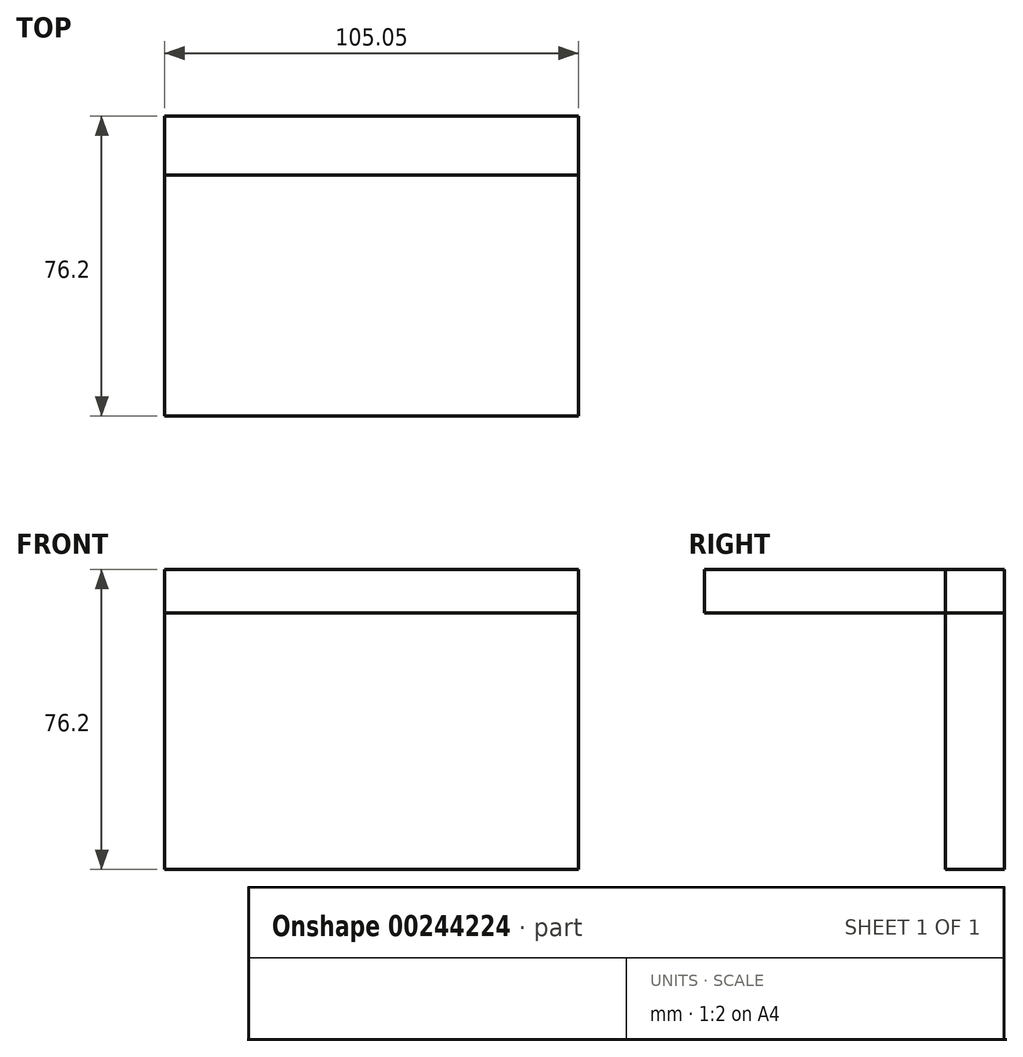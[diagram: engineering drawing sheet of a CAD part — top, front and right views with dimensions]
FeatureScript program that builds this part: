
annotation { "Feature Type Name" : "Feature", "Feature Type Description" : "" }
export const myFeature = defineFeature(function(context is Context, id is Id, definition is map)
    precondition{}
    {
        {
            var Q0;
            Q0=qCreatedBy(makeId("Front.planeOp"),FACE);
            var sketch = newSketch(context, id + "F0", { "sketchPlane" : qUnion([Q0])});
            skLineSegment(sketch, "E0.bottom", {"start": v(-63.6, 52.39) * mm, "end": v(41.45, 52.39) * mm});
            skLineSegment(sketch, "E0.top", {"start": v(-63.6, 41.31) * mm, "end": v(41.45, 41.31) * mm});
            skLineSegment(sketch, "E0.left", {"start": v(-63.6, 52.39) * mm, "end": v(-63.6, 41.31) * mm});
            skLineSegment(sketch, "E0.right", {"start": v(41.45, 52.39) * mm, "end": v(41.45, 41.31) * mm});
            skSolve(sketch);
        }
        {
            var Q0;
            Q0 = qSketchRegion(id + "F0", true);
            extrude(context, id + "F1", {"entities" : qUnion([Q0]), "depth" : 76.2 * mm});
        }
        {
            var Q0;
            Q0=makeQuery(id+"F1.opExtrude","SWEPT_FACE",FACE,{"disambiguationData":[OSD([sQuery(id+"F0.wireOp",EDGE,"E0.bottom")])]});
            var sketch = newSketch(context, id + "F2", { "sketchPlane" : qUnion([Q0])});
            skLineSegment(sketch, "E1.bottom", {"start": v(-63.6, 0) * mm, "end": v(41.45, 0) * mm});
            skLineSegment(sketch, "E1.top", {"start": v(-63.6, -14.96) * mm, "end": v(41.45, -14.96) * mm});
            skLineSegment(sketch, "E1.left", {"start": v(-63.6, 0) * mm, "end": v(-63.6, -14.96) * mm});
            skLineSegment(sketch, "E1.right", {"start": v(41.45, 0) * mm, "end": v(41.45, -14.96) * mm});
            skSolve(sketch);
        }
        {
            var Q0;
            Q0 = qSketchRegion(id + "F2", true);
            extrude(context, id + "F3", {"entities" : qUnion([Q0]), "oppositeDirection" : true, "depth" : 76.2 * mm});
        }
    });
